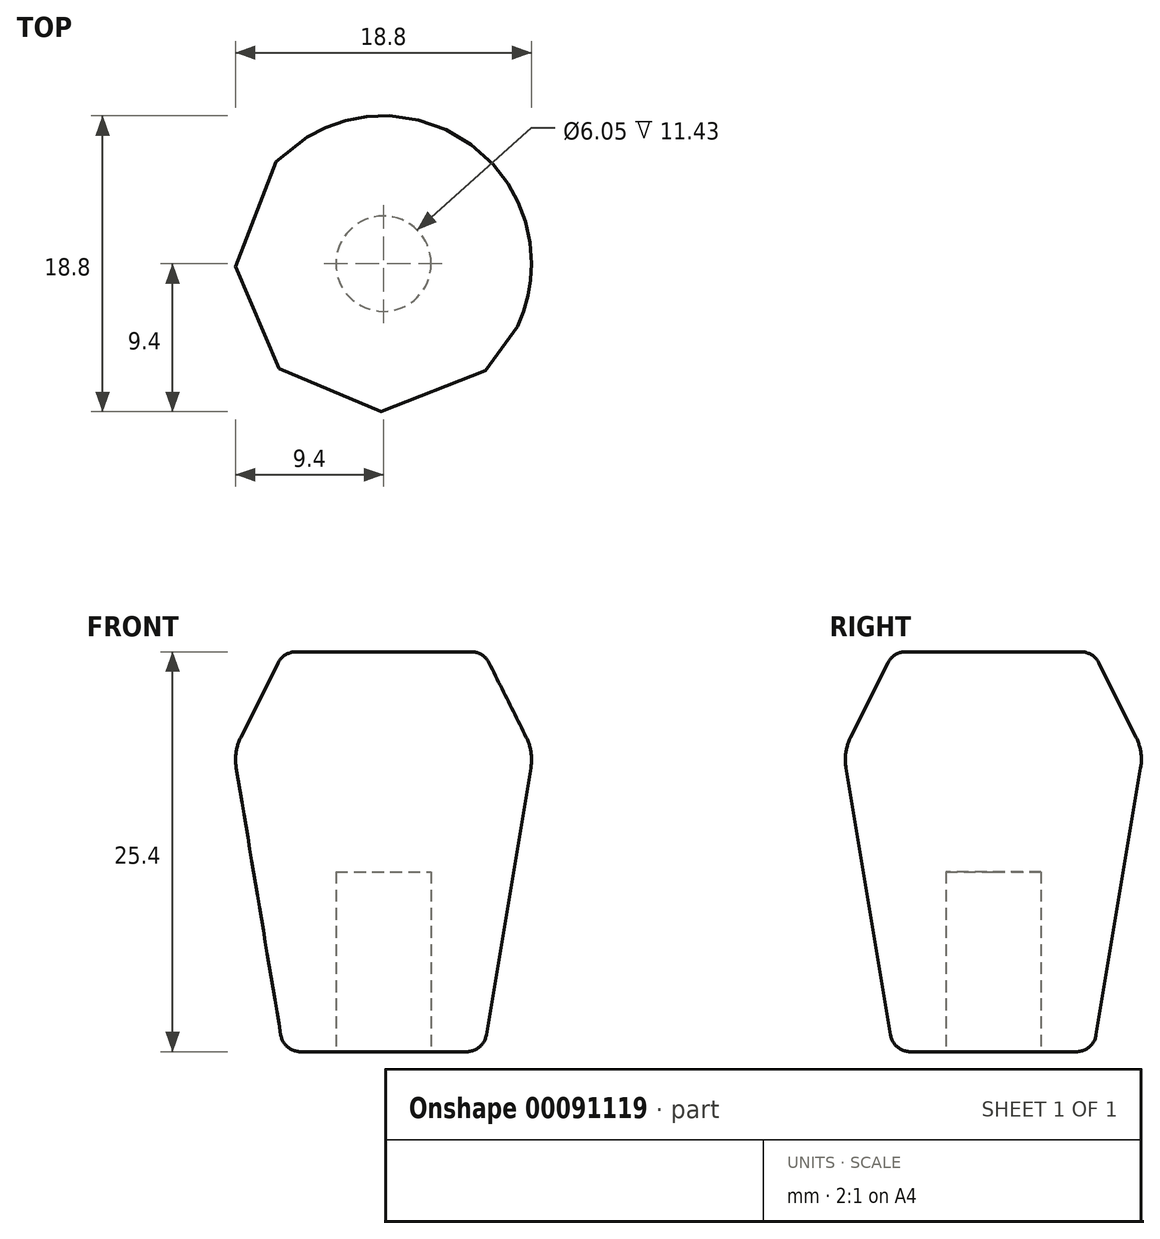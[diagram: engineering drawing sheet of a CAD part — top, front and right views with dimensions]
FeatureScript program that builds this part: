
annotation { "Feature Type Name" : "Feature", "Feature Type Description" : "" }
export const myFeature = defineFeature(function(context is Context, id is Id, definition is map)
    precondition{}
    {
        {
            var Q0;
            Q0=qCreatedBy(makeId("Front.planeOp"),FACE);
            var sketch = newSketch(context, id + "F0", { "sketchPlane" : qUnion([Q0])});
            skLineSegment(sketch, "E0", {"start": v(0, 0) * mm, "end": v(0, 25.4) * mm});
            skLineSegment(sketch, "E1", {"start": v(0, 0) * mm, "end": v(6.35, 0) * mm});
            skLineSegment(sketch, "E2", {"start": v(6.35, 0) * mm, "end": v(9.52, 19.05) * mm});
            skLineSegment(sketch, "E3", {"start": v(9.53, 19.05) * mm, "end": v(6.35, 25.4) * mm});
            skLineSegment(sketch, "E4", {"start": v(6.35, 25.4) * mm, "end": v(0, 25.4) * mm});
            skSolve(sketch);
        }
        {
            var Q0;
            Q0 = qSketchRegion(id + "F0", true);
            var Q1;
            Q1=sQuery(id+"F0.wireOp",EDGE,"E0");
            revolve(context, id + "F1", {"entities" : qUnion([Q0]), "axis" : qUnion([Q1]), "revolveType" : RevolveType.FULL});
        }
        {
            var Q0;
            Q0=makeQuery(id+"F1.opRevolve","SWEPT_FACE",FACE,{"disambiguationData":[OSD([sQuery(id+"F0.wireOp",EDGE,"E1")])]});
            var sketch = newSketch(context, id + "F2", { "sketchPlane" : qUnion([Q0])});
            skCircle(sketch, "E5", {"center": v(0, 0) * mm, "radius": 3.03 * mm});
            skSolve(sketch);
        }
        {
            var Q0;
            Q0 = qSketchRegion(id + "F2", true);
            extrude(context, id + "F3", {"entities" : qUnion([Q0]), "operationType" : NewBodyOperationType.REMOVE, "oppositeDirection" : true, "depth" : 11.43 * mm});
        }
        {
            var Q0;
            Q0=makeQuery(id+"F3.boolean.opBoolean","COPY",EDGE,{"derivedFrom":makeQuery(id+"F3.opExtrude","CAP_EDGE",EDGE,{"disambiguationData":[OSD([sQuery(id+"F2.wireOp",EDGE,"E5")])],"isStart":true})});
            var Q1;
            Q1=makeQuery(id+"F1.opRevolve","SWEPT_EDGE",EDGE,{"disambiguationData":[OSD([sQuery(id+"F0.wireOp",EDGE,"E3"),sQuery(id+"F0.wireOp",EDGE,"E4")])]});
            var Q2;
            Q2=makeQuery(id+"F1.opRevolve","SWEPT_EDGE",EDGE,{"disambiguationData":[OSD([sQuery(id+"F0.wireOp",EDGE,"E1"),sQuery(id+"F0.wireOp",EDGE,"E2")])]});
            fillet(context, id + "F4", {"entities" : qUnion([Q0, Q1, Q2]), "radius" : 1.27 * mm, "tangentPropagation" : true, "allowEdgeOverflow" : false});
        }
        {
            var Q0;
            Q0=makeQuery(id+"F1.opRevolve","SWEPT_EDGE",EDGE,{"disambiguationData":[OSD([sQuery(id+"F0.wireOp",EDGE,"E2"),sQuery(id+"F0.wireOp",EDGE,"E3")])]});
            fillet(context, id + "F5", {"entities" : qUnion([Q0]), "radius" : 3.17 * mm, "tangentPropagation" : true, "allowEdgeOverflow" : false});
        }
    });
